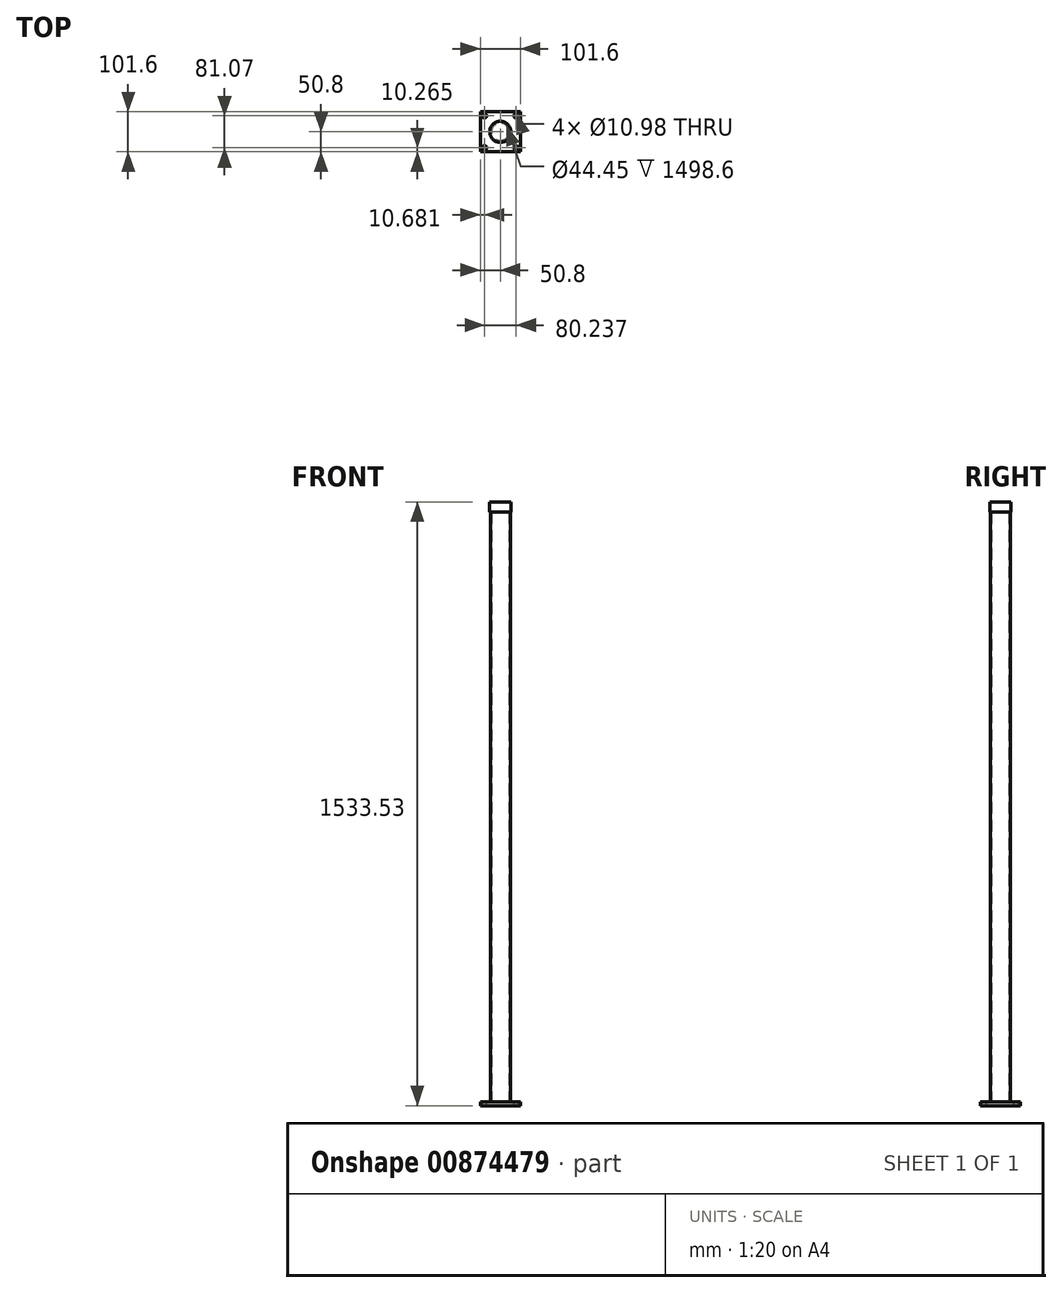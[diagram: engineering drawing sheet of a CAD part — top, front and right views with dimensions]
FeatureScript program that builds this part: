
annotation { "Feature Type Name" : "Feature", "Feature Type Description" : "" }
export const myFeature = defineFeature(function(context is Context, id is Id, definition is map)
    precondition{}
    {
        {
            var Q0;
            Q0=qCreatedBy(makeId("Top.planeOp"),FACE);
            var sketch = newSketch(context, id + "F0", { "sketchPlane" : qUnion([Q0])});
            skCircle(sketch, "E0", {"center": v(0, 0) * mm, "radius": 25.4 * mm});
            skCircle(sketch, "E1", {"center": v(0, 0) * mm, "radius": 22.23 * mm});
            skSolve(sketch);
        }
        {
            var Q0;
            Q0=makeQuery(id+"F0.imprint","IMPRINT",FACE,{"disambiguationData":[TD([[makeQuery(id+"F0.imprint","IMPRINT",EDGE,{"derivedFrom":sQuery(id+"F0.wireOp",EDGE,"E0")}),1.0]])]});
            extrude(context, id + "F1", {"entities" : qUnion([Q0]), "depth" : 1524 * mm, "offsetDistance" : 25.4 * mm});
        }
        {
            var Q0;
            Q0=qCreatedBy(makeId("Top.planeOp"),FACE);
            var sketch = newSketch(context, id + "F2", { "sketchPlane" : qUnion([Q0])});
            skLineSegment(sketch, "E2.bottom", {"start": v(-50.8, 50.8) * mm, "end": v(50.8, 50.8) * mm});
            skLineSegment(sketch, "E2.top", {"start": v(-50.8, -50.8) * mm, "end": v(50.8, -50.8) * mm});
            skLineSegment(sketch, "E2.left", {"start": v(-50.8, 50.8) * mm, "end": v(-50.8, -50.8) * mm});
            skLineSegment(sketch, "E2.right", {"start": v(50.8, 50.8) * mm, "end": v(50.8, -50.8) * mm});
            skPoint(sketch, "E2.middle", {"position": v(0, 0) * mm});
            skCircle(sketch, "E3", {"center": v(40.12, 40.53) * mm, "radius": 5.49 * mm});
            skCircle(sketch, "E4.MirrorC", {"center": v(-40.12, 40.53) * mm, "radius": 5.49 * mm});
            skCircle(sketch, "E5.MirrorC", {"center": v(-40.12, -40.53) * mm, "radius": 5.49 * mm});
            skCircle(sketch, "E6.MirrorC", {"center": v(40.12, -40.53) * mm, "radius": 5.49 * mm});
            skSolve(sketch);
        }
        {
            var Q0;
            Q0=makeQuery(id+"F2.imprint","IMPRINT",FACE,{"disambiguationData":[TD([[makeQuery(id+"F2.imprint","IMPRINT",EDGE,{"derivedFrom":sQuery(id+"F2.wireOp",EDGE,"E2.bottom")}),-1.0]])]});
            extrude(context, id + "F3", {"entities" : qUnion([Q0]), "operationType" : NewBodyOperationType.ADD, "oppositeDirection" : true, "depth" : 9.52 * mm, "offsetDistance" : 25.4 * mm});
        }
        {
            var Q0;
            Q0=makeQuery(id+"F1.opExtrude","CAP_FACE",FACE,{"disambiguationData":[OSD([sQuery(id+"F0.wireOp",EDGE,"E0"),sQuery(id+"F0.wireOp",EDGE,"E1")])],"isStart":false});
            var sketch = newSketch(context, id + "F4", { "sketchPlane" : qUnion([Q0])});
            skCircle(sketch, "E7", {"center": v(0, 0) * mm, "radius": 26.8 * mm});
            skSolve(sketch);
        }
        {
            var Q0;
            Q0=qSketchRegion(id+"F4",true);
            extrude(context, id + "F5", {"entities" : qUnion([Q0]), "operationType" : NewBodyOperationType.ADD, "oppositeDirection" : true, "depth" : 25.4 * mm, "offsetDistance" : 25.4 * mm});
        }
    });
